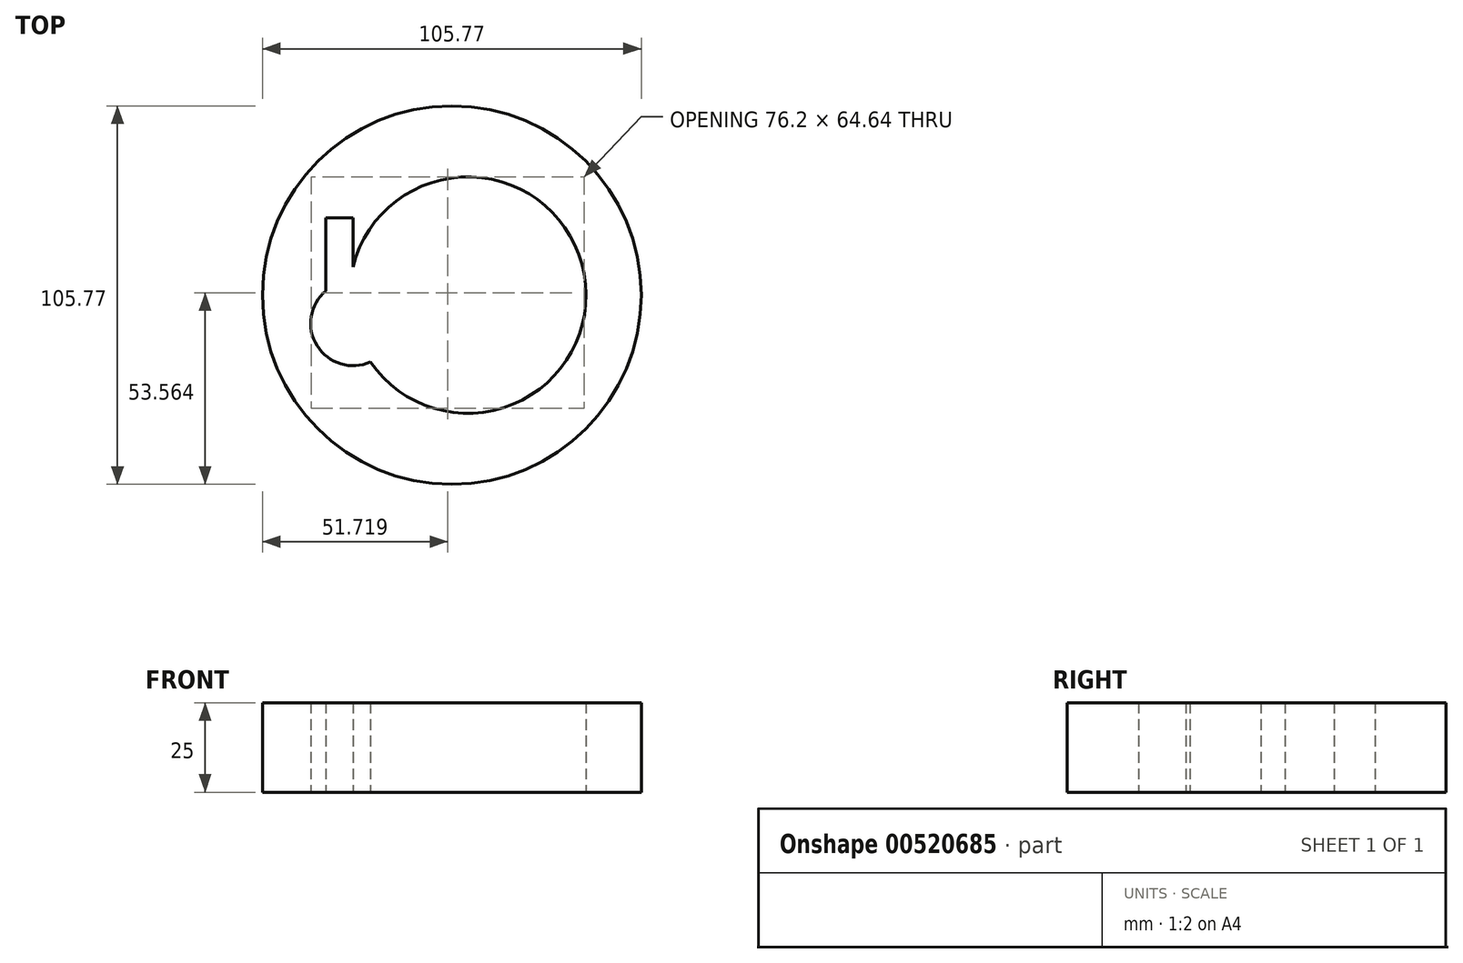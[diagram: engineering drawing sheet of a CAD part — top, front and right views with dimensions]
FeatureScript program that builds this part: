
annotation { "Feature Type Name" : "Feature", "Feature Type Description" : "" }
export const myFeature = defineFeature(function(context is Context, id is Id, definition is map)
    precondition{}
    {
        {
            var Q0;
            Q0=qCreatedBy(makeId("Top.planeOp"),FACE);
            var sketch = newSketch(context, id + "F0", { "sketchPlane" : qUnion([Q0])});
            skCircle(sketch, "E0", {"center": v(-60.44, 15.28) * mm, "radius": 52.88 * mm});
            skCircle(sketch, "E1", {"center": v(-60.44, 15.28) * mm, "radius": 12.79 * mm});
            skCircle(sketch, "E2", {"center": v(-55.98, 15.28) * mm, "radius": 33.01 * mm});
            skCircle(sketch, "E3", {"center": v(-34.58, 15.28) * mm, "radius": 11.6 * mm});
            skSolve(sketch);
        }
        {
            var Q0;
            Q0 = qSketchRegion(id + "F0", true);
            extrude(context, id + "F1", {"entities" : qUnion([Q0]), "depth" : 25 * mm, "offsetDistance" : 25 * mm});
        }
        {
            var Q0;
            Q0=makeQuery(id+"F1.opExtrude","CAP_FACE",FACE,{"disambiguationData":[OSD([sQuery(id+"F0.wireOp",EDGE,"E0"),sQuery(id+"F0.wireOp",EDGE,"E2")])],"isStart":true});
            var sketch = newSketch(context, id + "F2", { "sketchPlane" : qUnion([Q0])});
            skLineSegment(sketch, "E4.bottom", {"start": v(-88.03, -7.38) * mm, "end": v(-95.6, -7.38) * mm});
            skLineSegment(sketch, "E4.top", {"start": v(-88.03, -36.9) * mm, "end": v(-95.6, -36.9) * mm});
            skLineSegment(sketch, "E4.left", {"start": v(-88.03, -7.38) * mm, "end": v(-88.03, -36.9) * mm});
            skLineSegment(sketch, "E4.right", {"start": v(-95.6, -7.38) * mm, "end": v(-95.6, -36.9) * mm});
            skSolve(sketch);
        }
        {
            var Q0;
            Q0 = qSketchRegion(id + "F2", true);
            extrude(context, id + "F3", {"entities" : qUnion([Q0]), "operationType" : NewBodyOperationType.REMOVE, "oppositeDirection" : true, "depth" : 25 * mm, "offsetDistance" : 25 * mm});
        }
        {
            var Q0;
            Q0=makeQuery(id+"F1.opExtrude","CAP_FACE",FACE,{"disambiguationData":[OSD([sQuery(id+"F0.wireOp",EDGE,"E0"),sQuery(id+"F0.wireOp",EDGE,"E2")])],"isStart":true});
            var sketch = newSketch(context, id + "F4", { "sketchPlane" : qUnion([Q0])});
            skCircle(sketch, "E5", {"center": v(-88.03, -7.38) * mm, "radius": 11.81 * mm});
            skSolve(sketch);
        }
        {
            var Q0;
            Q0 = qSketchRegion(id + "F4", true);
            extrude(context, id + "F5", {"entities" : qUnion([Q0]), "operationType" : NewBodyOperationType.REMOVE, "oppositeDirection" : true, "depth" : 25 * mm, "offsetDistance" : 25 * mm});
        }
    });
